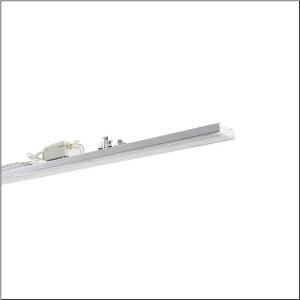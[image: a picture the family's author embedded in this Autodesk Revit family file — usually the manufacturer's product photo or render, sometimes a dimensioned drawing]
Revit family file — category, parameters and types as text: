
# Revit family: licross_21_recessed_ho_51te12vn4axm
name_source: partatom
category: Lighting Fixtures
units: mm (PartAtom-declared; Revit-internal decimal feet)

## family parameters
Cut with Voids When Loaded = No
Host = Face
Light Source = No
Part Type = Normal
Room Calculation Point = No
Round Connector Dimension = Use Diameter
Shared = No

## types (1)
- --- (1 x LED, 10000 lm, 53.4 W, 4000K)
    Apparent Load = 53 VA
    CIE Flux Codes = 66 91 98 100 100
    Color Rendering = 80
    Color Temperature = 4000K
    Default Elevation = 1800 mm
    Description = Licross 21 Recessed HO, luminaire insert, of sheet steel, galvanised, coil coated, white, length: 1.500mm, width: 66mm, height: 67mm, LED rated luminous flux: 10.000lm, light colour: 840, SDCM (Standard Deviation of Colour Matching)MacAdam ≤ 2 SDCM (initial), control gear: DALI 2, CLO, with plug, 5-pole, with phase selection, mains connection: 220..240V, AC, 50/60Hz, start of lifetime: 53W, end of service life: 59W, internal wiring halogen-free, primary optical cover: cover, of PMMA, light emission: direct distribution, primary light characteristic: symmetric, protection rating (complete): IP54, insulation class (complete): insulation class I (protective earthing), certification: CE, ENEC, VDE, UKCA, protection symbol: D if used in an environment with non-conductive dust loads with corresponding accessories, impact resistance: IK06, permissible ambient temperature for indoor applications: -25..+35°C, corresponds to IFS (International Featured Standards) requirements for safety and quality in the food industry, reducing of maximum allowable ambient temperature of 5°C with ceiling mounting, LABS conformity tested according to VDMA 24364:2018-05, The light source and the operating device comply with the requirements of the Ecodesign Regulation (EU) 2019/2020 and are replaceable in accordance with this regulation, packaging unit: 1 piece
    Height = 58 mm
    Lamp = 1 x LED
    Lamp Light Flux = 10000 lm
    Lamp Power = 53.4 W
    Lamp count = 1
    Length = 1500 mm
    Luminous efficacy = 187 lm/W
    Manufacturer = Siteco
    ModVariant = No
    Model = 51TE12VN4AXM
    Mounting Place = Ceiling
    Mounting Type = Pendant
    Number of Poles = 1
    OnlyDefault = Yes
    Power Factor = 1
    Product Name = Licross 21 Recessed HO
    Product group = luminaire insert | ceiling pendant
    ProductGroupID = 901
    Protection Class = Protection class I
    Protection Degree = IP 54
    RLX_Detail_Level = 1
    RLX_Emergency_Light_Flux = 0 lm
    RLX_Emergency_Type = 0
    RLX_Emergency_Type_DB = No
    RlxData = <blob elided: 24837 chars, md5=ba7aae4b>
    Socket = socket
    Standby Power = 0 W
    System Light Flux = 10000 lm
    System Power = 53 W
    Type Comments = factory setting: luminous flux: 100 % | dim-lin: 254 | 364 mA
    Type Image = l_1296930.jpg
    URL = http://relux.com
    VarID = @adj_000379
    Voltage = 0 V
    Weight = 0.00 kg
    Width = 66 mm

## geometry (parser evidence)
native form markers: Blend x4, Sweep x11
no freeform markers — native parametric forms only
